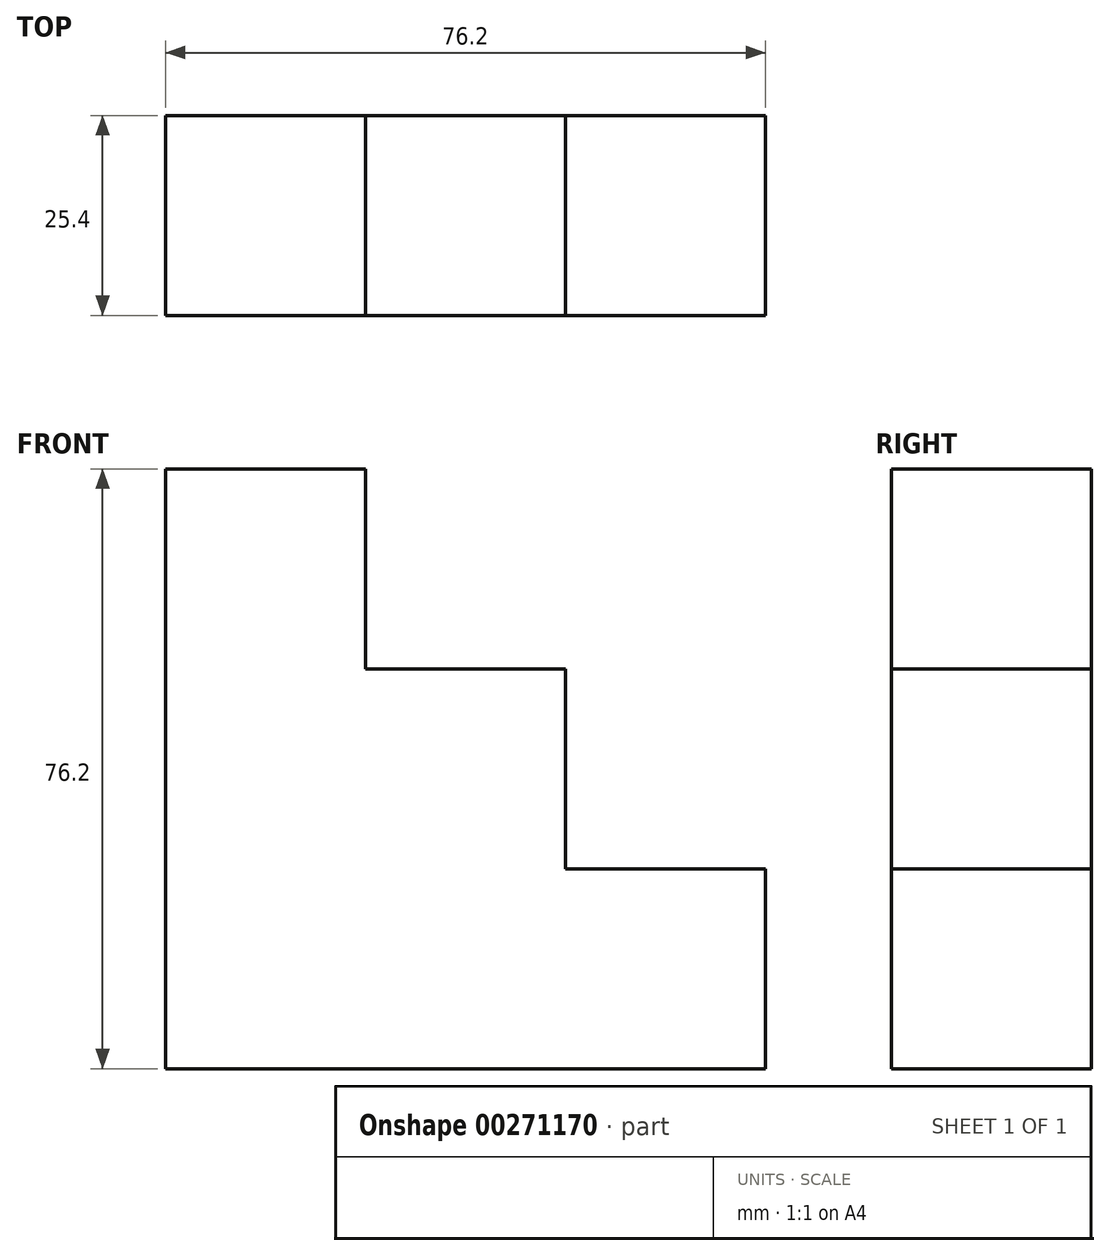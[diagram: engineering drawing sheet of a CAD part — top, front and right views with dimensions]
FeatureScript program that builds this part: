
annotation { "Feature Type Name" : "Feature", "Feature Type Description" : "" }
export const myFeature = defineFeature(function(context is Context, id is Id, definition is map)
    precondition{}
    {
        {
            var Q0;
            Q0=qCreatedBy(makeId("Front.planeOp"),FACE);
            var sketch = newSketch(context, id + "F0", { "sketchPlane" : qUnion([Q0])});
            skLineSegment(sketch, "E0", {"start": v(0, 0) * mm, "end": v(-76.2, 0) * mm});
            skLineSegment(sketch, "E1", {"start": v(-76.2, 0) * mm, "end": v(-76.2, 76.2) * mm});
            skLineSegment(sketch, "E2", {"start": v(-76.2, 76.2) * mm, "end": v(-50.8, 76.2) * mm});
            skLineSegment(sketch, "E3", {"start": v(-50.8, 76.2) * mm, "end": v(-50.8, 50.8) * mm});
            skLineSegment(sketch, "E4", {"start": v(-50.8, 50.8) * mm, "end": v(-25.4, 50.8) * mm});
            skLineSegment(sketch, "E5", {"start": v(-25.4, 50.8) * mm, "end": v(-25.4, 25.4) * mm});
            skLineSegment(sketch, "E6", {"start": v(-25.4, 25.4) * mm, "end": v(0, 25.4) * mm});
            skLineSegment(sketch, "E7", {"start": v(0, 25.4) * mm, "end": v(0, 0) * mm});
            skSolve(sketch);
        }
        {
            var Q0;
            Q0 = qSketchRegion(id + "F0", true);
            extrude(context, id + "F1", {"entities" : qUnion([Q0]), "depth" : 25.4 * mm});
        }
    });
